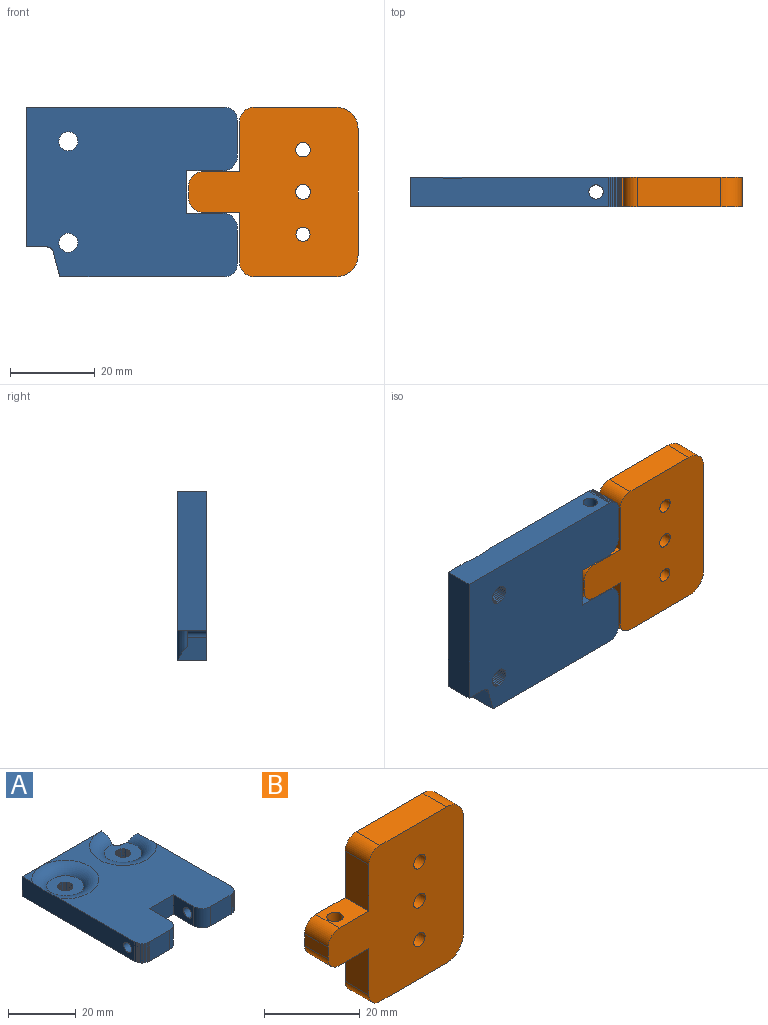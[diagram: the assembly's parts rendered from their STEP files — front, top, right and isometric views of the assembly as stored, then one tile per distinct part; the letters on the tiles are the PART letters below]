
ASSEMBLY  parts=2 mates=1
PART A: 113 faces, bbox 53.2x54.7x7.2 mm
  f0: plane 4.5x0.4mm, normal (-1,0.09,0), area 1.8mm2, adj f1,f34,f73,f109
  f1: plane 4.5x0.4mm, normal (-1,-0.09,0), area 1.8mm2, adj f0,f2,f73,f109
  f2: plane 4.5x0.39mm, normal (-0.96,-0.27,0), area 1.8mm2, adj f1,f3,f73,f109
  f3: plane 4.5x0.36mm, normal (-0.9,-0.43,0), area 1.8mm2, adj f2,f4,f73,f109
  f4: plane 4.5x0.33mm, normal (-0.81,-0.59,0), area 1.8mm2, adj f3,f5,f73,f109
  f5: plane 4.5x0.29mm, normal (-0.69,-0.72,0), area 1.8mm2, adj f4,f6,f73,f109
  f6: plane 4.5x0.34mm, normal (-0.55,-0.83,0), area 1.8mm2, adj f5,f7,f73,f109
  f7: plane 4.5x0.37mm, normal (-0.39,-0.92,0), area 1.8mm2, adj f6,f8,f73,f109
  f8: plane 4.5x0.39mm, normal (-0.22,-0.97,0), area 1.8mm2, adj f7,f9,f73,f109
  f9: plane 4.5x0.4mm, normal (-0.04,-1,0), area 1.8mm2, adj f8,f10,f73,f109
  f10: plane 4.5x0.4mm, normal (0.13,-0.99,0), area 1.8mm2, adj f9,f11,f73,f109
  f11: plane 4.5x0.38mm, normal (0.31,-0.95,0), area 1.8mm2, adj f10,f12,f73,f109
  f12: plane 4.5x0.36mm, normal (0.47,-0.88,0), area 1.8mm2, adj f11,f13,f73,f109
  f13: plane 4.5x0.32mm, normal (0.62,-0.78,0), area 1.8mm2, adj f12,f14,f73,f109
  f14: plane 4.5x0.3mm, normal (0.75,-0.66,0), area 1.8mm2, adj f13,f15,f73,f109
  f15: plane 4.5x0.35mm, normal (0.86,-0.51,0), area 1.8mm2, adj f14,f16,f73,f109
  f16: plane 4.5x0.38mm, normal (0.94,-0.35,0), area 1.8mm2, adj f15,f17,f73,f109
  f17: plane 4.5x0.4mm, normal (0.98,-0.18,0), area 1.8mm2, adj f16,f18,f73,f109
  f18: plane 4.5x0.4mm, normal (1,0,0), area 1.8mm2, adj f17,f19,f73,f109
  f19: plane 4.5x0.4mm, normal (0.98,0.18,0), area 1.8mm2, adj f18,f20,f73,f109
  f20: plane 4.5x0.38mm, normal (0.94,0.35,0), area 1.8mm2, adj f19,f21,f73,f109
  f21: plane 4.5x0.35mm, normal (0.86,0.51,0), area 1.8mm2, adj f20,f22,f73,f109
  f22: plane 4.5x0.3mm, normal (0.75,0.66,0), area 1.8mm2, adj f21,f23,f73,f109
  f23: plane 4.5x0.32mm, normal (0.62,0.78,0), area 1.8mm2, adj f22,f24,f73,f109
  f24: plane 4.5x0.36mm, normal (0.47,0.88,0), area 1.8mm2, adj f23,f25,f73,f109
  f25: plane 4.5x0.38mm, normal (0.31,0.95,0), area 1.8mm2, adj f24,f26,f73,f109
  f26: plane 4.5x0.4mm, normal (0.13,0.99,0), area 1.8mm2, adj f25,f27,f73,f109
  f27: plane 4.5x0.4mm, normal (-0.04,1,0), area 1.8mm2, adj f26,f28,f73,f109
  f28: plane 4.5x0.39mm, normal (-0.22,0.97,0), area 1.8mm2, adj f27,f29,f73,f109
  f29: plane 4.5x0.37mm, normal (-0.39,0.92,0), area 1.8mm2, adj f28,f30,f73,f109
  f30: plane 4.5x0.34mm, normal (-0.55,0.83,0), area 1.8mm2, adj f29,f31,f73,f109
  f31: plane 4.5x0.29mm, normal (-0.69,0.72,0), area 1.8mm2, adj f30,f32,f73,f109
  f32: plane 4.5x0.33mm, normal (-0.81,0.59,0), area 1.8mm2, adj f31,f33,f73,f109
  f33: plane 4.5x0.36mm, normal (-0.9,0.43,0), area 1.8mm2, adj f32,f34,f73,f109
  f34: plane 4.5x0.39mm, normal (-0.96,0.27,0), area 1.8mm2, adj f0,f33,f73,f109
  f35: plane 4.5x0.4mm, normal (-1,0.09,0), area 1.8mm2, adj f36,f69,f73,f110
  f36: plane 4.5x0.4mm, normal (-1,-0.09,0), area 1.8mm2, adj f35,f37,f73,f110
  f37: plane 4.5x0.39mm, normal (-0.96,-0.27,0), area 1.8mm2, adj f36,f38,f73,f110
  f38: plane 4.5x0.36mm, normal (-0.9,-0.43,0), area 1.8mm2, adj f37,f39,f73,f110
  f39: plane 4.5x0.33mm, normal (-0.81,-0.59,0), area 1.8mm2, adj f38,f40,f73,f110
  f40: plane 4.5x0.29mm, normal (-0.69,-0.72,0), area 1.8mm2, adj f39,f41,f73,f110
  f41: plane 4.5x0.34mm, normal (-0.55,-0.83,0), area 1.8mm2, adj f40,f42,f73,f110
  f42: plane 4.5x0.37mm, normal (-0.39,-0.92,0), area 1.8mm2, adj f41,f43,f73,f110
  f43: plane 4.5x0.39mm, normal (-0.22,-0.97,0), area 1.8mm2, adj f42,f44,f73,f110
  f44: plane 4.5x0.4mm, normal (-0.04,-1,0), area 1.8mm2, adj f43,f45,f73,f110
  f45: plane 4.5x0.4mm, normal (0.13,-0.99,0), area 1.8mm2, adj f44,f46,f73,f110
  f46: plane 4.5x0.38mm, normal (0.31,-0.95,0), area 1.8mm2, adj f45,f47,f73,f110
  f47: plane 4.5x0.36mm, normal (0.47,-0.88,0), area 1.8mm2, adj f46,f48,f73,f110
  f48: plane 4.5x0.32mm, normal (0.62,-0.78,0), area 1.8mm2, adj f47,f49,f73,f110
  f49: plane 4.5x0.3mm, normal (0.75,-0.66,0), area 1.8mm2, adj f48,f50,f73,f110
  f50: plane 4.5x0.35mm, normal (0.86,-0.51,0), area 1.8mm2, adj f49,f51,f73,f110
  f51: plane 4.5x0.38mm, normal (0.94,-0.35,0), area 1.8mm2, adj f50,f52,f73,f110
  f52: plane 4.5x0.4mm, normal (0.98,-0.18,0), area 1.8mm2, adj f51,f53,f73,f110
  f53: plane 4.5x0.4mm, normal (1,0,0), area 1.8mm2, adj f52,f54,f73,f110
  f54: plane 4.5x0.4mm, normal (0.98,0.18,0), area 1.8mm2, adj f53,f55,f73,f110
  f55: plane 4.5x0.38mm, normal (0.94,0.35,0), area 1.8mm2, adj f54,f56,f73,f110
  f56: plane 4.5x0.35mm, normal (0.86,0.51,0), area 1.8mm2, adj f55,f57,f73,f110
  f57: plane 4.5x0.3mm, normal (0.75,0.66,0), area 1.8mm2, adj f56,f58,f73,f110
  f58: plane 4.5x0.32mm, normal (0.62,0.78,0), area 1.8mm2, adj f57,f59,f73,f110
  f59: plane 4.5x0.36mm, normal (0.47,0.88,0), area 1.8mm2, adj f58,f60,f73,f110
  f60: plane 4.5x0.38mm, normal (0.31,0.95,0), area 1.8mm2, adj f59,f61,f73,f110
  f61: plane 4.5x0.4mm, normal (0.13,0.99,0), area 1.8mm2, adj f60,f62,f73,f110
  f62: plane 4.5x0.4mm, normal (-0.04,1,0), area 1.8mm2, adj f61,f63,f73,f110
  f63: plane 4.5x0.39mm, normal (-0.22,0.97,0), area 1.8mm2, adj f62,f64,f73,f110
  f64: plane 4.5x0.37mm, normal (-0.39,0.92,0), area 1.8mm2, adj f63,f65,f73,f110
  f65: plane 4.5x0.34mm, normal (-0.55,0.83,0), area 1.8mm2, adj f64,f66,f73,f110
  f66: plane 4.5x0.29mm, normal (-0.69,0.72,0), area 1.8mm2, adj f65,f67,f73,f110
  f67: plane 4.5x0.33mm, normal (-0.81,0.59,0), area 1.8mm2, adj f66,f68,f73,f110
  f68: plane 4.5x0.36mm, normal (-0.9,0.43,0), area 1.8mm2, adj f67,f69,f73,f110
  f69: plane 4.5x0.39mm, normal (-0.96,0.27,0), area 1.8mm2, adj f35,f68,f73,f110
  f70: cylinder r=1.5mm len=4.5mm, axis (0,0,1), area 10.6mm2, adj f73,f76,f77,f110
  f71: plane 8.5x7mm, normal (0,-1,0), area 59.5mm2, adj f73,f78,f79,f108
  f72: plane 39x7mm, normal (1,0,0), area 262.3mm2, adj f73,f77,f78,f91,f106,f111
  f73: plane 50x40mm, normal (0,0,-1), area 1790.1mm2, adj f0,f1,f2,f3,f4,f5,f6,f7
  f74: plane 47x7mm, normal (-1,0,0), area 317.9mm2, adj f73,f75,f78,f89,f105,f112
  f75: plane 33x7mm, normal (0,1,0), area 231mm2, adj f73,f74,f76,f78
  f76: plane 7.09x5.09mm, normal (1,0,0), area 30.8mm2, adj f70,f73,f75,f78,f110,f111
  f77: plane 6.97x5.73mm, normal (0.26,0.96,0), area 30.3mm2, adj f70,f72,f73,f110,f111
  f78: plane 50x40mm, normal (0,0,1), area 1281.1mm2, adj f71,f72,f74,f75,f76,f79,f80,f81
  f79: plane 7x0.43mm, normal (-0.07,-1,0), area 3mm2, adj f71,f73,f78,f80
  f80: plane 7x0.42mm, normal (-0.21,-0.98,0), area 3mm2, adj f73,f78,f79,f81
  f81: plane 7x0.4mm, normal (-0.35,-0.94,0), area 3mm2, adj f73,f78,f80,f82
  f82: plane 7x0.38mm, normal (-0.48,-0.88,0), area 3mm2, adj f73,f78,f81,f83
  f83: plane 7x0.34mm, normal (-0.6,-0.8,0), area 3mm2, adj f73,f78,f82,f84
  f84: plane 7x0.3mm, normal (-0.71,-0.71,0), area 3mm2, adj f73,f78,f83,f85
  f85: plane 7x0.34mm, normal (-0.8,-0.6,0), area 3mm2, adj f73,f78,f84,f86
  f86: plane 7x0.38mm, normal (-0.88,-0.48,0), area 3mm2, adj f73,f78,f85,f87
  f87: plane 7x0.4mm, normal (-0.94,-0.35,0), area 3mm2, adj f73,f78,f86,f88
  f88: plane 7x0.42mm, normal (-0.98,-0.21,0), area 3mm2, adj f73,f78,f87,f89
  f89: plane 7x0.43mm, normal (-1,-0.07,0), area 3mm2, adj f73,f74,f78,f88
  f90: plane 8.5x7mm, normal (0,-1,0), area 59.5mm2, adj f73,f78,f101,f107
  f91: plane 7x0.43mm, normal (1,-0.07,0), area 3mm2, adj f72,f73,f78,f92
  f92: plane 7x0.42mm, normal (0.98,-0.21,0), area 3mm2, adj f73,f78,f91,f93
  f93: plane 7x0.4mm, normal (0.94,-0.35,0), area 3mm2, adj f73,f78,f92,f94
  f94: plane 7x0.38mm, normal (0.88,-0.48,0), area 3mm2, adj f73,f78,f93,f95
  f95: plane 7x0.34mm, normal (0.8,-0.6,0), area 3mm2, adj f73,f78,f94,f96
  f96: plane 7x0.3mm, normal (0.71,-0.71,0), area 3mm2, adj f73,f78,f95,f97
  f97: plane 7x0.34mm, normal (0.6,-0.8,0), area 3mm2, adj f73,f78,f96,f98
  f98: plane 7x0.38mm, normal (0.48,-0.88,0), area 3mm2, adj f73,f78,f97,f99
  f99: plane 7x0.4mm, normal (0.35,-0.94,0), area 3mm2, adj f73,f78,f98,f100
  f100: plane 7x0.42mm, normal (0.21,-0.98,0), area 3mm2, adj f73,f78,f99,f101
  f101: plane 7x0.43mm, normal (0.07,-1,0), area 3mm2, adj f73,f78,f90,f100
  f102: plane 8.5x7mm, normal (-1,0,0), area 50.4mm2, adj f73,f78,f103,f106,f107
  f103: plane 10x7mm, normal (0,-1,0), area 70mm2, adj f73,f78,f102,f104
  f104: plane 8.5x7mm, normal (1,0,0), area 50.4mm2, adj f73,f78,f103,f105,f108
  f105: cylinder r=1.7mm len=15mm, axis (1,0,0), area 160.2mm2, adj f74,f104
  f106: cylinder r=1.7mm len=15mm, axis (1,0,0), area 160.2mm2, adj f72,f102
  f107: cylinder r=3.5mm len=7mm, axis (0,0,-1), area 38.5mm2, adj f73,f78,f90,f102
  f108: cylinder r=3.5mm len=7mm, axis (0,0,1), area 38.5mm2, adj f71,f73,f78,f104
  f109: plane 11x11mm, normal (0,0,1), area 79.2mm2, adj f0,f1,f2,f3,f4,f5,f6,f7
  f110: plane 11x11mm, normal (0,0,1), area 75.2mm2, adj f35,f36,f37,f38,f39,f40,f41,f42
  f111: torus R=9.83mm, axis (0,0,1), area 191mm2, adj f72,f76,f77,f78,f110
  f112: torus R=9.83mm, axis (0,0,1), area 230.4mm2, adj f74,f78,f109
PART B: 20 faces, bbox 40x7x40 mm
  f0: plane 19.7x7mm, normal (0,0,1), area 137.9mm2, adj f8,f9,f10,f19
  f1: plane 11.9x7mm, normal (-1,0,0), area 83.3mm2, adj f2,f8,f9,f10
  f2: plane 8.7x7mm, normal (0,0,1), area 51.8mm2, adj f1,f8,f9,f11,f14
  f3: plane 7x3mm, normal (-1,0,0), area 21mm2, adj f8,f9,f11,f12
  f4: plane 8.7x7mm, normal (0,0,-1), area 51.8mm2, adj f5,f8,f9,f12,f14
  f5: plane 11.9x7mm, normal (-1,0,0), area 83.3mm2, adj f4,f8,f9,f13
  f6: plane 19.7x7mm, normal (0,0,-1), area 137.9mm2, adj f8,f9,f13,f18
  f7: plane 30x7mm, normal (1,0,0), area 210mm2, adj f8,f9,f18,f19
  f8: plane 40x40mm, normal (0,-1,0), area 1187.5mm2, adj f0,f1,f2,f3,f4,f5,f6,f7
  f9: plane 40x40mm, normal (0,1,0), area 1187.5mm2, adj f0,f1,f2,f3,f4,f5,f6,f7
  f10: cylinder r=3.3mm len=7mm, axis (0,-1,0), area 36.3mm2, adj f0,f1,f8,f9
  f11: cylinder r=3.3mm len=7mm, axis (0,-1,0), area 36.3mm2, adj f2,f3,f8,f9
  f12: cylinder r=3.3mm len=7mm, axis (0,1,0), area 36.3mm2, adj f3,f4,f8,f9
  f13: cylinder r=3.3mm len=7mm, axis (0,1,0), area 36.3mm2, adj f5,f6,f8,f9
  f14: cylinder r=1.7mm len=9.6mm, axis (0,0,1), area 102.5mm2, adj f2,f4
  f15: cylinder r=1.75mm len=7mm, axis (0,-1,0), area 77mm2, adj f8,f9
  f16: cylinder r=1.71mm len=7mm, axis (0,-1,0), area 75.4mm2, adj f8,f9
  f17: cylinder r=1.67mm len=7mm, axis (0,-1,0), area 73.3mm2, adj f8,f9
  f18: cylinder r=5mm len=7mm, axis (0,-1,0), area 55mm2, adj f6,f7,f8,f9
  f19: cylinder r=5mm len=7mm, axis (0,1,0), area 55mm2, adj f0,f7,f8,f9
PLACE A rot(axis=(-0.58,0.58,0.58),120deg) t=(-10.79,-4.09,-10.16)mm
PLACE B t=(27.71,2.91,-10.16)mm
MATE cylindrical A.f105 <-> B.f14  axis (0,0,-1) through (13.21,-0.59,-5.16)mm
